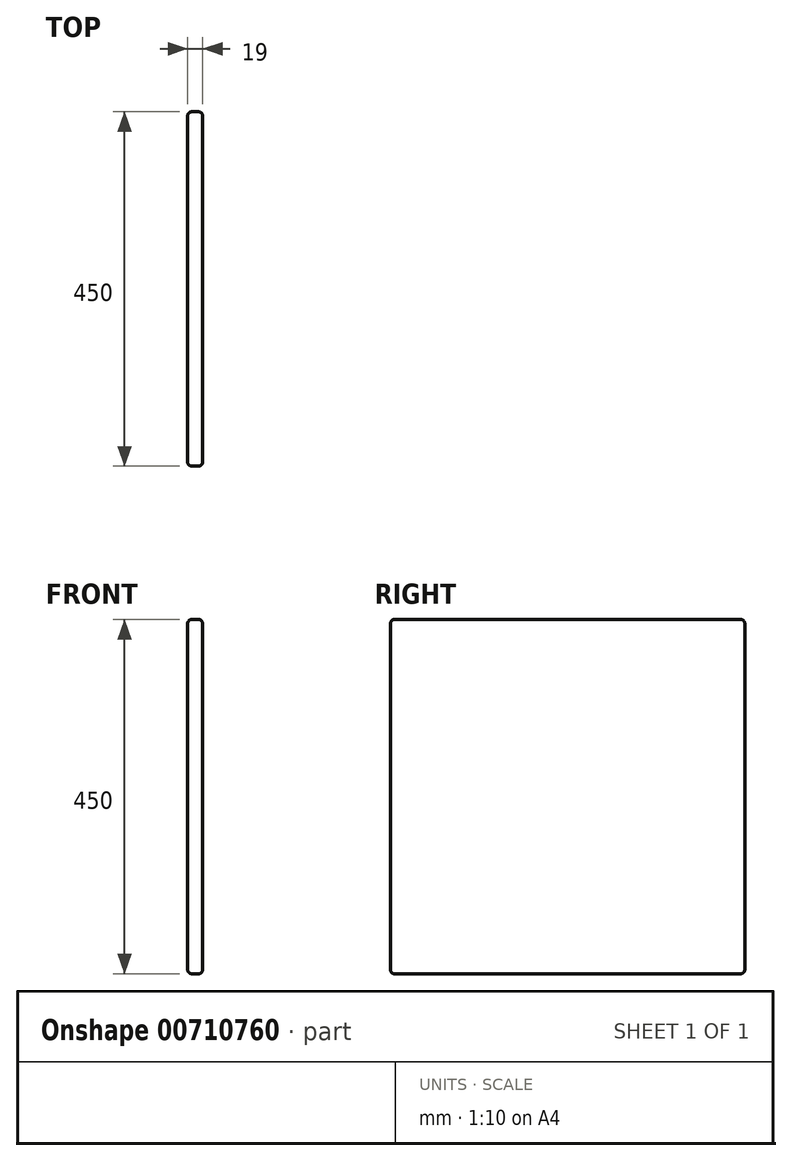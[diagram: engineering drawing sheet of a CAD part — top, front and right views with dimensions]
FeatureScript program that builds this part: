
annotation { "Feature Type Name" : "Feature", "Feature Type Description" : "" }
export const myFeature = defineFeature(function(context is Context, id is Id, definition is map)
    precondition{}
    {
        {
            var Q0;
            Q0=qCreatedBy(makeId("Right.planeOp"),FACE);
            var sketch = newSketch(context, id + "F0", { "sketchPlane" : qUnion([Q0])});
            skLineSegment(sketch, "E0.bottom", {"start": v(-33.4, 467.11) * mm, "end": v(416.6, 467.11) * mm});
            skLineSegment(sketch, "E0.top", {"start": v(-33.4, 17.11) * mm, "end": v(416.6, 17.11) * mm});
            skLineSegment(sketch, "E0.left", {"start": v(-33.4, 467.11) * mm, "end": v(-33.4, 17.11) * mm});
            skLineSegment(sketch, "E0.right", {"start": v(416.6, 467.11) * mm, "end": v(416.6, 17.11) * mm});
            skSolve(sketch);
        }
        {
            var Q0;
            Q0=makeQuery(id+"F0.imprint","IMPRINT",FACE,{"disambiguationData":[TD([[makeQuery(id+"F0.imprint","IMPRINT",EDGE,{"derivedFrom":sQuery(id+"F0.wireOp",EDGE,"E0.bottom")}),-1.0]])]});
            extrude(context, id + "F1", {"entities" : qUnion([Q0]), "depth" : 19 * mm, "offsetDistance" : 25.4 * mm});
        }
        {
            var Q0;
            Q0=makeQuery(id+"F1.opExtrude","SWEPT_EDGE",EDGE,{"disambiguationData":[OSD([sQuery(id+"F0.wireOp",EDGE,"E0.bottom"),sQuery(id+"F0.wireOp",EDGE,"E0.left")])]});
            var Q1;
            Q1=makeQuery(id+"F1.opExtrude","SWEPT_EDGE",EDGE,{"disambiguationData":[OSD([sQuery(id+"F0.wireOp",EDGE,"E0.bottom"),sQuery(id+"F0.wireOp",EDGE,"E0.right")])]});
            var Q2;
            Q2=makeQuery(id+"F1.opExtrude","SWEPT_EDGE",EDGE,{"disambiguationData":[OSD([sQuery(id+"F0.wireOp",EDGE,"E0.top"),sQuery(id+"F0.wireOp",EDGE,"E0.right")])]});
            var Q3;
            Q3=makeQuery(id+"F1.opExtrude","SWEPT_EDGE",EDGE,{"disambiguationData":[OSD([sQuery(id+"F0.wireOp",EDGE,"E0.top"),sQuery(id+"F0.wireOp",EDGE,"E0.left")])]});
            var Q4;
            Q4=makeQuery(id+"F1.opExtrude","CAP_EDGE",EDGE,{"disambiguationData":[OSD([sQuery(id+"F0.wireOp",EDGE,"E0.left")])],"isStart":false});
            var Q5;
            Q5=makeQuery(id+"F1.opExtrude","CAP_EDGE",EDGE,{"disambiguationData":[OSD([sQuery(id+"F0.wireOp",EDGE,"E0.left")])],"isStart":true});
            var Q6;
            Q6=makeQuery(id+"F1.opExtrude","CAP_EDGE",EDGE,{"disambiguationData":[OSD([sQuery(id+"F0.wireOp",EDGE,"E0.top")])],"isStart":false});
            var Q7;
            Q7=makeQuery(id+"F1.opExtrude","CAP_EDGE",EDGE,{"disambiguationData":[OSD([sQuery(id+"F0.wireOp",EDGE,"E0.top")])],"isStart":true});
            var Q8;
            Q8=makeQuery(id+"F1.opExtrude","CAP_EDGE",EDGE,{"disambiguationData":[OSD([sQuery(id+"F0.wireOp",EDGE,"E0.right")])],"isStart":false});
            var Q9;
            Q9=makeQuery(id+"F1.opExtrude","CAP_EDGE",EDGE,{"disambiguationData":[OSD([sQuery(id+"F0.wireOp",EDGE,"E0.right")])],"isStart":true});
            var Q10;
            Q10=makeQuery(id+"F1.opExtrude","CAP_EDGE",EDGE,{"disambiguationData":[OSD([sQuery(id+"F0.wireOp",EDGE,"E0.bottom")])],"isStart":false});
            var Q11;
            Q11=makeQuery(id+"F1.opExtrude","CAP_EDGE",EDGE,{"disambiguationData":[OSD([sQuery(id+"F0.wireOp",EDGE,"E0.bottom")])],"isStart":true});
            fillet(context, id + "F2", {"entities" : qUnion([Q0, Q1, Q2, Q3, Q4, Q5, Q6, Q7, Q8, Q9, Q10, Q11]), "radius" : 5 * mm, "tangentPropagation" : true, "allowEdgeOverflow" : false});
        }
    });
